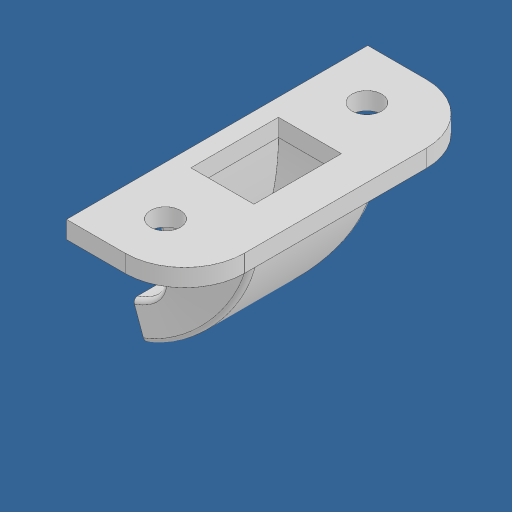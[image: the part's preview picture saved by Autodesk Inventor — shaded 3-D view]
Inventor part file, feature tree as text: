
AUTODESK INVENTOR PART (.ipt)
format: ipt  version: 2024.2 (Build 282272000, 272)  size: 240,640 bytes
history: native  units: mm
features: sketch x4, plane x3, fillet x2, loft x2, extrude x1, hole x1, other x1
ambient origin geometry x8: Origin, YZ Plane, XZ Plane, XY Plane, X Axis, Y Axis, Z Axis, Center Point
bodies: Solid1 (feature_tree)
feature tree (14):
  extrude  "Extrusion1"  Depth=13.5mm
  fillet  "Fillet1"  Radius=2.0mm
  sketch  "Sketch2"  dims[d4=6.8mm d5=10.0mm]
  plane  "Work Plane2"
  plane  "Work Plane3"
  sketch  "Sketch3"  dims[d6=2.0mm d7=7.2mm d8=2.0mm]
  loft  "Loft1"
  loft  "Loft2"
  fillet  "Fillet2"  Radius=2.0mm
  hole  "Hole1"  [1 undecoded]
  sketch  "Sketch1"  dims[d0=34.4mm d1=13.5mm d2=2.0mm d3=0.0mm]
  plane  "Work Plane1"
  other  "Work Axis1"
  sketch  "Sketch4"  dims[d9=2.0mm d10=2.0mm d11=-20.0mm d12=-10.0mm d13=3.490659mm d14=4.0mm d15=10.0mm d16=1.0mm d18=2.0mm d19=2.0mm d20=1.0mm d21=10.0mm d22=90.0deg d23=10.0mm d24=90.0deg d25=10.0mm d26=90.0deg d27=10.0mm d28=90.0deg d29=2.0mm d30=10.0mm d31=7.2mm d32=0.5mm d33=11.5mm d34=11.5mm d35=3.4mm d36=6.0mm d37=6.3mm d38=2.0mm d39=90.0deg d40=8.0mm d41=20.594885mm]
note: 1 required parameter value undecoded (feature->parameter linkage not recoverable at this tier; creation-order binding heuristic only, values carry confidence <= 0.55)
